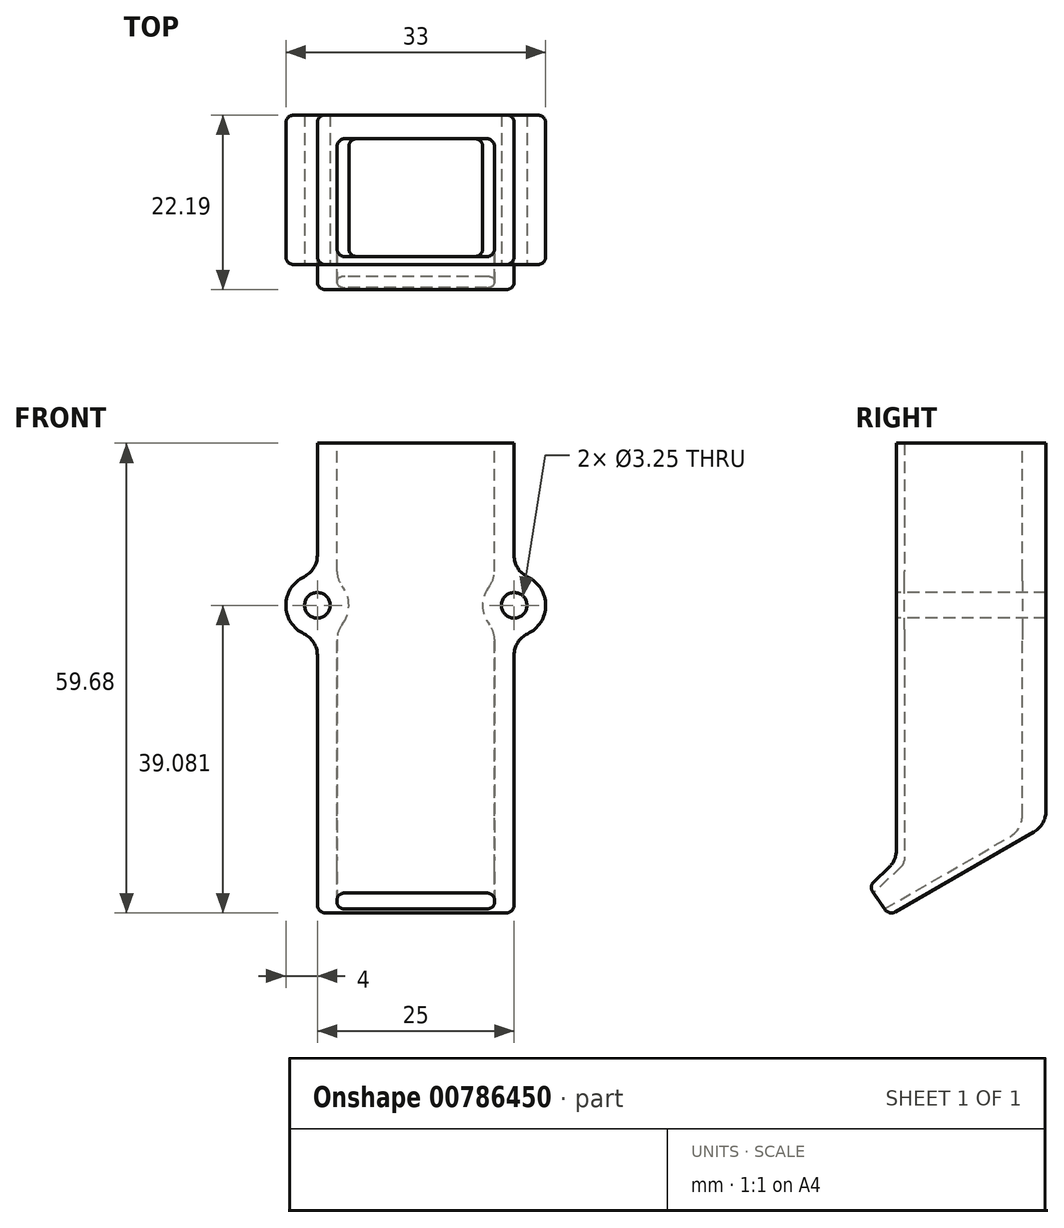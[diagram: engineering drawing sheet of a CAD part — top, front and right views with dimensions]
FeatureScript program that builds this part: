
annotation { "Feature Type Name" : "Feature", "Feature Type Description" : "" }
export const myFeature = defineFeature(function(context is Context, id is Id, definition is map)
    precondition{}
    {
        {
            var Q0;
            Q0=qCreatedBy(makeId("Right.planeOp"),FACE);
            var sketch = newSketch(context, id + "F0", { "sketchPlane" : qUnion([Q0])});
            skLineSegment(sketch, "E0", {"start": v(10.5, 0) * mm, "end": v(10.5, -48.5) * mm});
            skLineSegment(sketch, "E1", {"start": v(-8.5, 0) * mm, "end": v(-8.5, -53) * mm});
            skLineSegment(sketch, "E2", {"start": v(10.5, 0) * mm, "end": v(-8.5, 0) * mm});
            skLineSegment(sketch, "E3", {"start": v(-8.5, -53) * mm, "end": v(-12, -56.31) * mm});
            skLineSegment(sketch, "E4", {"start": v(-12, -56.31) * mm, "end": v(-9.42, -60) * mm});
            skLineSegment(sketch, "E5", {"start": v(-9.42, -60) * mm, "end": v(10.5, -48.5) * mm});
            skLineSegment(sketch, "E6", {"start": v(0, 3.25) * mm, "end": v(0, -60.76) * mm, "construction": true});
            skSolve(sketch);
        }
        {
            var Q0;
            Q0 = qSketchRegion(id + "F0", true);
            extrude(context, id + "F1", {"entities" : qUnion([Q0]), "endBound" : BoundingType.SYMMETRIC, "depth" : 25 * mm, "offsetDistance" : 25 * mm});
        }
        {
            var Q0;
            Q0=qCreatedBy(makeId("Right.planeOp"),FACE);
            var sketch = newSketch(context, id + "F2", { "sketchPlane" : qUnion([Q0])});
            skLineSegment(sketch, "E7", {"start": v(-7.5, 0) * mm, "end": v(-7.5, -53.43) * mm});
            skLineSegment(sketch, "E8", {"start": v(-7.5, -53.43) * mm, "end": v(-11.42, -57.14) * mm});
            skLineSegment(sketch, "E9", {"start": v(-11.42, -57.14) * mm, "end": v(-10, -59.18) * mm});
            skLineSegment(sketch, "E10", {"start": v(-10, -59.18) * mm, "end": v(7.5, -49.08) * mm});
            skLineSegment(sketch, "E11", {"start": v(7.5, -49.08) * mm, "end": v(7.5, 0) * mm});
            skLineSegment(sketch, "E12", {"start": v(7.5, 0) * mm, "end": v(-7.5, 0) * mm});
            skSolve(sketch);
        }
        {
            var Q0;
            Q0 = qSketchRegion(id + "F2", true);
            extrude(context, id + "F3", {"entities" : qUnion([Q0]), "operationType" : NewBodyOperationType.REMOVE, "endBound" : BoundingType.SYMMETRIC, "depth" : 20 * mm, "offsetDistance" : 25 * mm});
        }
        {
            var Q0;
            Q0=makeQuery(id+"F1.opExtrude","SWEPT_FACE",FACE,{"disambiguationData":[OSD([sQuery(id+"F0.wireOp",EDGE,"E1")])]});
            var sketch = newSketch(context, id + "F4", { "sketchPlane" : qUnion([Q0])});
            skCircle(sketch, "E13", {"center": v(12.5, -20.6) * mm, "radius": 4 * mm});
            skCircle(sketch, "E14", {"center": v(-12.5, -20.6) * mm, "radius": 4 * mm});
            skLineSegment(sketch, "E15", {"start": v(0, 4.77) * mm, "end": v(0, -64.34) * mm, "construction": true});
            skSolve(sketch);
        }
        {
            var Q0;
            Q0 = qSketchRegion(id + "F4", true);
            var Q1;
            Q1=makeQuery(id+"F1.opExtrude","SWEPT_FACE",FACE,{"disambiguationData":[OSD([sQuery(id+"F0.wireOp",EDGE,"E0")])]});
            extrude(context, id + "F5", {"entities" : qUnion([Q0]), "operationType" : NewBodyOperationType.ADD, "endBound" : BoundingType.UP_TO_SURFACE, "oppositeDirection" : true, "depth" : 25 * mm, "endBoundEntityFace" : qUnion([Q1]), "offsetDistance" : 25 * mm});
        }
        {
            var Q0;
            Q0=makeQuery(id+"F5.boolean.opBoolean","MERGE",FACE,{"derivedFrom":[makeQuery(id+"F1.opExtrude","SWEPT_FACE",FACE,{"disambiguationData":[OSD([sQuery(id+"F0.wireOp",EDGE,"E1")])]}),makeQuery(id+"F5.opExtrude","CAP_FACE",FACE,{"disambiguationData":[OSD([sQuery(id+"F4.wireOp",EDGE,"E13")])],"isStart":true}),makeQuery(id+"F5.opExtrude","CAP_FACE",FACE,{"disambiguationData":[OSD([sQuery(id+"F4.wireOp",EDGE,"E14")])],"isStart":true})]});
            var sketch = newSketch(context, id + "F6", { "sketchPlane" : qUnion([Q0])});
            skCircle(sketch, "E16.0", {"center": v(-12.5, -20.6) * mm, "radius": 1.62 * mm});
            skCircle(sketch, "E17.0", {"center": v(12.5, -20.6) * mm, "radius": 1.62 * mm});
            skSolve(sketch);
        }
        {
            var Q0;
            Q0 = qSketchRegion(id + "F6", true);
            var Q1;
            Q1=makeQuery(id+"F5.boolean.opBoolean","MERGE",FACE,{"derivedFrom":[makeQuery(id+"F1.opExtrude","SWEPT_FACE",FACE,{"disambiguationData":[OSD([sQuery(id+"F0.wireOp",EDGE,"E0")])]}),makeQuery(id+"F5.opExtrude","CAP_FACE",FACE,{"disambiguationData":[OSD([sQuery(id+"F4.wireOp",EDGE,"E13")])],"isStart":false}),makeQuery(id+"F5.opExtrude","CAP_FACE",FACE,{"disambiguationData":[OSD([sQuery(id+"F4.wireOp",EDGE,"E14")])],"isStart":false})]});
            extrude(context, id + "F7", {"entities" : qUnion([Q0]), "operationType" : NewBodyOperationType.REMOVE, "endBound" : BoundingType.UP_TO_SURFACE, "oppositeDirection" : true, "depth" : 25 * mm, "endBoundEntityFace" : qUnion([Q1]), "offsetDistance" : 25 * mm});
        }
        {
            var Q0;
            Q0=makeQuery(id+"F5.boolean.opBoolean","INTERSECT",EDGE,{"disambiguationData":[OD(0.0)],"derivedFrom":[makeQuery(id+"F1.opExtrude","CAP_FACE",FACE,{"disambiguationData":[OSD([sQuery(id+"F0.wireOp",EDGE,"E0"),sQuery(id+"F0.wireOp",EDGE,"E1"),sQuery(id+"F0.wireOp",EDGE,"E2"),sQuery(id+"F0.wireOp",EDGE,"E3"),sQuery(id+"F0.wireOp",EDGE,"E4"),sQuery(id+"F0.wireOp",EDGE,"E5")])],"isStart":true}),makeQuery(id+"F5.opExtrude","SWEPT_FACE",FACE,{"disambiguationData":[OSD([sQuery(id+"F4.wireOp",EDGE,"E14")])]})]});
            var Q1;
            Q1=makeQuery(id+"F5.boolean.opBoolean","INTERSECT",EDGE,{"disambiguationData":[OD(1.0)],"derivedFrom":[makeQuery(id+"F1.opExtrude","CAP_FACE",FACE,{"disambiguationData":[OSD([sQuery(id+"F0.wireOp",EDGE,"E0"),sQuery(id+"F0.wireOp",EDGE,"E1"),sQuery(id+"F0.wireOp",EDGE,"E2"),sQuery(id+"F0.wireOp",EDGE,"E3"),sQuery(id+"F0.wireOp",EDGE,"E4"),sQuery(id+"F0.wireOp",EDGE,"E5")])],"isStart":true}),makeQuery(id+"F5.opExtrude","SWEPT_FACE",FACE,{"disambiguationData":[OSD([sQuery(id+"F4.wireOp",EDGE,"E14")])]})]});
            var Q2;
            Q2=makeQuery(id+"F5.boolean.opBoolean","INTERSECT",EDGE,{"disambiguationData":[OD(0.0)],"derivedFrom":[makeQuery(id+"F1.opExtrude","CAP_FACE",FACE,{"disambiguationData":[OSD([sQuery(id+"F0.wireOp",EDGE,"E0"),sQuery(id+"F0.wireOp",EDGE,"E1"),sQuery(id+"F0.wireOp",EDGE,"E2"),sQuery(id+"F0.wireOp",EDGE,"E3"),sQuery(id+"F0.wireOp",EDGE,"E4"),sQuery(id+"F0.wireOp",EDGE,"E5")])],"isStart":false}),makeQuery(id+"F5.opExtrude","SWEPT_FACE",FACE,{"disambiguationData":[OSD([sQuery(id+"F4.wireOp",EDGE,"E13")])]})]});
            var Q3;
            Q3=makeQuery(id+"F5.boolean.opBoolean","INTERSECT",EDGE,{"disambiguationData":[OD(1.0)],"derivedFrom":[makeQuery(id+"F1.opExtrude","CAP_FACE",FACE,{"disambiguationData":[OSD([sQuery(id+"F0.wireOp",EDGE,"E0"),sQuery(id+"F0.wireOp",EDGE,"E1"),sQuery(id+"F0.wireOp",EDGE,"E2"),sQuery(id+"F0.wireOp",EDGE,"E3"),sQuery(id+"F0.wireOp",EDGE,"E4"),sQuery(id+"F0.wireOp",EDGE,"E5")])],"isStart":false}),makeQuery(id+"F5.opExtrude","SWEPT_FACE",FACE,{"disambiguationData":[OSD([sQuery(id+"F4.wireOp",EDGE,"E13")])]})]});
            var Q4;
            Q4=makeQuery(id+"F5.boolean.opBoolean","INTERSECT",EDGE,{"disambiguationData":[OD(1.0)],"derivedFrom":[makeQuery(id+"F3.boolean.opBoolean","COPY",FACE,{"derivedFrom":makeQuery(id+"F3.opExtrude","CAP_FACE",FACE,{"disambiguationData":[OSD([sQuery(id+"F2.wireOp",EDGE,"E7"),sQuery(id+"F2.wireOp",EDGE,"E8"),sQuery(id+"F2.wireOp",EDGE,"E9"),sQuery(id+"F2.wireOp",EDGE,"E10"),sQuery(id+"F2.wireOp",EDGE,"E11"),sQuery(id+"F2.wireOp",EDGE,"E12")])],"isStart":true})}),makeQuery(id+"F5.opExtrude","SWEPT_FACE",FACE,{"disambiguationData":[OSD([sQuery(id+"F4.wireOp",EDGE,"E14")])]})]});
            var Q5;
            Q5=makeQuery(id+"F5.boolean.opBoolean","INTERSECT",EDGE,{"disambiguationData":[OD(1.0)],"derivedFrom":[makeQuery(id+"F3.boolean.opBoolean","COPY",FACE,{"derivedFrom":makeQuery(id+"F3.opExtrude","CAP_FACE",FACE,{"disambiguationData":[OSD([sQuery(id+"F2.wireOp",EDGE,"E7"),sQuery(id+"F2.wireOp",EDGE,"E8"),sQuery(id+"F2.wireOp",EDGE,"E9"),sQuery(id+"F2.wireOp",EDGE,"E10"),sQuery(id+"F2.wireOp",EDGE,"E11"),sQuery(id+"F2.wireOp",EDGE,"E12")])],"isStart":false})}),makeQuery(id+"F5.opExtrude","SWEPT_FACE",FACE,{"disambiguationData":[OSD([sQuery(id+"F4.wireOp",EDGE,"E13")])]})]});
            var Q6;
            Q6=makeQuery(id+"F5.boolean.opBoolean","INTERSECT",EDGE,{"disambiguationData":[OD(0.0)],"derivedFrom":[makeQuery(id+"F3.boolean.opBoolean","COPY",FACE,{"derivedFrom":makeQuery(id+"F3.opExtrude","CAP_FACE",FACE,{"disambiguationData":[OSD([sQuery(id+"F2.wireOp",EDGE,"E7"),sQuery(id+"F2.wireOp",EDGE,"E8"),sQuery(id+"F2.wireOp",EDGE,"E9"),sQuery(id+"F2.wireOp",EDGE,"E10"),sQuery(id+"F2.wireOp",EDGE,"E11"),sQuery(id+"F2.wireOp",EDGE,"E12")])],"isStart":false})}),makeQuery(id+"F5.opExtrude","SWEPT_FACE",FACE,{"disambiguationData":[OSD([sQuery(id+"F4.wireOp",EDGE,"E13")])]})]});
            var Q7;
            Q7=makeQuery(id+"F5.boolean.opBoolean","INTERSECT",EDGE,{"disambiguationData":[OD(0.0)],"derivedFrom":[makeQuery(id+"F3.boolean.opBoolean","COPY",FACE,{"derivedFrom":makeQuery(id+"F3.opExtrude","CAP_FACE",FACE,{"disambiguationData":[OSD([sQuery(id+"F2.wireOp",EDGE,"E7"),sQuery(id+"F2.wireOp",EDGE,"E8"),sQuery(id+"F2.wireOp",EDGE,"E9"),sQuery(id+"F2.wireOp",EDGE,"E10"),sQuery(id+"F2.wireOp",EDGE,"E11"),sQuery(id+"F2.wireOp",EDGE,"E12")])],"isStart":true})}),makeQuery(id+"F5.opExtrude","SWEPT_FACE",FACE,{"disambiguationData":[OSD([sQuery(id+"F4.wireOp",EDGE,"E14")])]})]});
            var Q8;
            Q8=makeQuery(id+"F3.boolean.opBoolean","COPY",EDGE,{"derivedFrom":makeQuery(id+"F3.opExtrude","SWEPT_EDGE",EDGE,{"disambiguationData":[OSD([sQuery(id+"F2.wireOp",EDGE,"E10"),sQuery(id+"F2.wireOp",EDGE,"E11")])]})});
            var Q9;
            Q9=makeQuery(id+"F1.opExtrude","SWEPT_EDGE",EDGE,{"disambiguationData":[OSD([sQuery(id+"F0.wireOp",EDGE,"E1"),sQuery(id+"F0.wireOp",EDGE,"E3")])]});
            var Q10;
            Q10=makeQuery(id+"F1.opExtrude","SWEPT_EDGE",EDGE,{"disambiguationData":[OSD([sQuery(id+"F0.wireOp",EDGE,"E0"),sQuery(id+"F0.wireOp",EDGE,"E5")])]});
            fillet(context, id + "F8", {"entities" : qUnion([Q0, Q1, Q2, Q3, Q4, Q5, Q6, Q7, Q8, Q9, Q10]), "tangentPropagation" : true, "radius" : 3 * mm, "defaultsChanged" : false, "vertexSettings" : [], "allowEdgeOverflow" : false});
        }
        {
            var Q0;
            {var subQ0=sQuery(id+"F2.wireOp",EDGE,"E7");Q0=makeQuery(id+"F5.boolean.opBoolean","SPLIT",EDGE,{"disambiguationData":[TD([makeQuery(id+"F1.opExtrude","SWEPT_FACE",FACE,{"disambiguationData":[OSD([sQuery(id+"F0.wireOp",EDGE,"E2")])]})])],"derivedFrom":makeQuery(id+"F3.boolean.opBoolean","COPY",EDGE,{"derivedFrom":makeQuery(id+"F3.opExtrude","CAP_EDGE",EDGE,{"disambiguationData":[OSD([subQ0])],"isStart":false})})});}
            var Q1;
            {var subQ0=sQuery(id+"F2.wireOp",EDGE,"E7");Q1=makeQuery(id+"F5.boolean.opBoolean","SPLIT",EDGE,{"disambiguationData":[TD([makeQuery(id+"F1.opExtrude","SWEPT_FACE",FACE,{"disambiguationData":[OSD([sQuery(id+"F0.wireOp",EDGE,"E2")])]})])],"derivedFrom":makeQuery(id+"F3.boolean.opBoolean","COPY",EDGE,{"derivedFrom":makeQuery(id+"F3.opExtrude","CAP_EDGE",EDGE,{"disambiguationData":[OSD([subQ0])],"isStart":true})})});}
            var Q2;
            {var subQ0=sQuery(id+"F2.wireOp",EDGE,"E11");Q2=makeQuery(id+"F5.boolean.opBoolean","SPLIT",EDGE,{"disambiguationData":[TD([makeQuery(id+"F1.opExtrude","SWEPT_FACE",FACE,{"disambiguationData":[OSD([sQuery(id+"F0.wireOp",EDGE,"E2")])]})])],"derivedFrom":makeQuery(id+"F3.boolean.opBoolean","COPY",EDGE,{"derivedFrom":makeQuery(id+"F3.opExtrude","CAP_EDGE",EDGE,{"disambiguationData":[OSD([subQ0])],"isStart":false})})});}
            var Q3;
            {var subQ0=sQuery(id+"F2.wireOp",EDGE,"E11");Q3=makeQuery(id+"F5.boolean.opBoolean","SPLIT",EDGE,{"disambiguationData":[TD([makeQuery(id+"F1.opExtrude","SWEPT_FACE",FACE,{"disambiguationData":[OSD([sQuery(id+"F0.wireOp",EDGE,"E2")])]})])],"derivedFrom":makeQuery(id+"F3.boolean.opBoolean","COPY",EDGE,{"derivedFrom":makeQuery(id+"F3.opExtrude","CAP_EDGE",EDGE,{"disambiguationData":[OSD([subQ0])],"isStart":true})})});}
            var Q4;
            Q4=makeQuery(id+"F3.boolean.opBoolean","COPY",EDGE,{"derivedFrom":makeQuery(id+"F3.opExtrude","CAP_EDGE",EDGE,{"disambiguationData":[OSD([sQuery(id+"F2.wireOp",EDGE,"E10")])],"isStart":true})});
            var Q5;
            Q5=makeQuery(id+"F3.boolean.opBoolean","COPY",EDGE,{"derivedFrom":makeQuery(id+"F3.opExtrude","CAP_EDGE",EDGE,{"disambiguationData":[OSD([sQuery(id+"F2.wireOp",EDGE,"E10")])],"isStart":false})});
            var Q6;
            Q6=makeQuery(id+"F3.boolean.opBoolean","COPY",EDGE,{"derivedFrom":makeQuery(id+"F3.opExtrude","CAP_EDGE",EDGE,{"disambiguationData":[OSD([sQuery(id+"F2.wireOp",EDGE,"E8")])],"isStart":false})});
            var Q7;
            Q7=makeQuery(id+"F3.boolean.opBoolean","COPY",EDGE,{"derivedFrom":makeQuery(id+"F3.opExtrude","CAP_EDGE",EDGE,{"disambiguationData":[OSD([sQuery(id+"F2.wireOp",EDGE,"E8")])],"isStart":true})});
            var Q8;
            Q8=makeQuery(id+"F3.boolean.opBoolean","COPY",EDGE,{"derivedFrom":makeQuery(id+"F3.opExtrude","SWEPT_EDGE",EDGE,{"disambiguationData":[OSD([sQuery(id+"F2.wireOp",EDGE,"E7"),sQuery(id+"F2.wireOp",EDGE,"E8")])]})});
            var Q9;
            {var subQ0=sQuery(id+"F0.wireOp",EDGE,"E3");var subQ1=sQuery(id+"F0.wireOp",EDGE,"E1");var subQ2=makeQuery(id+"F1.opExtrude","SWEPT_FACE",FACE,{"disambiguationData":[OSD([subQ1])]});var subQ4=makeQuery(id+"F1.opExtrude","CAP_FACE",FACE,{"disambiguationData":[OSD([sQuery(id+"F0.wireOp",EDGE,"E0"),subQ1,sQuery(id+"F0.wireOp",EDGE,"E2"),subQ0,sQuery(id+"F0.wireOp",EDGE,"E4"),sQuery(id+"F0.wireOp",EDGE,"E5")])],"isStart":true});Q9=makeQuery(id+"F5.boolean.opBoolean","SPLIT",EDGE,{"disambiguationData":[topologyDisambiguationEdgeConnected([subQ4,subQ2]),TD([makeQuery(id+"F1.opExtrude","SWEPT_FACE",FACE,{"disambiguationData":[OSD([subQ0])]})])],"derivedFrom":makeQuery(id+"F1.opExtrude","CAP_EDGE",EDGE,{"disambiguationData":[OSD([subQ1])],"isStart":true})});}
            var Q10;
            Q10=makeQuery(id+"F5.opExtrude","CAP_EDGE",EDGE,{"disambiguationData":[OSD([sQuery(id+"F4.wireOp",EDGE,"E14")])],"isStart":true});
            var Q11;
            {var subQ0=sQuery(id+"F0.wireOp",EDGE,"E2");var subQ1=sQuery(id+"F0.wireOp",EDGE,"E1");var subQ2=makeQuery(id+"F1.opExtrude","SWEPT_FACE",FACE,{"disambiguationData":[OSD([subQ1])]});var subQ4=makeQuery(id+"F1.opExtrude","CAP_FACE",FACE,{"disambiguationData":[OSD([sQuery(id+"F0.wireOp",EDGE,"E0"),subQ1,subQ0,sQuery(id+"F0.wireOp",EDGE,"E3"),sQuery(id+"F0.wireOp",EDGE,"E4"),sQuery(id+"F0.wireOp",EDGE,"E5")])],"isStart":true});Q11=makeQuery(id+"F5.boolean.opBoolean","SPLIT",EDGE,{"disambiguationData":[topologyDisambiguationEdgeConnected([subQ4,subQ2]),TD([makeQuery(id+"F1.opExtrude","SWEPT_FACE",FACE,{"disambiguationData":[OSD([subQ0])]})])],"derivedFrom":makeQuery(id+"F1.opExtrude","CAP_EDGE",EDGE,{"disambiguationData":[OSD([subQ1])],"isStart":true})});}
            var Q12;
            Q12=makeQuery(id+"F1.opExtrude","CAP_EDGE",EDGE,{"disambiguationData":[OSD([sQuery(id+"F0.wireOp",EDGE,"E4")])],"isStart":true});
            var Q13;
            Q13=makeQuery(id+"F1.opExtrude","CAP_EDGE",EDGE,{"disambiguationData":[OSD([sQuery(id+"F0.wireOp",EDGE,"E5")])],"isStart":true});
            var Q14;
            {var subQ0=sQuery(id+"F0.wireOp",EDGE,"E5");var subQ1=sQuery(id+"F0.wireOp",EDGE,"E0");Q14=makeQuery(id+"F5.boolean.opBoolean","SPLIT",EDGE,{"disambiguationData":[TD([makeQuery(id+"F1.opExtrude","SWEPT_FACE",FACE,{"disambiguationData":[OSD([subQ0])]})])],"derivedFrom":makeQuery(id+"F1.opExtrude","CAP_EDGE",EDGE,{"disambiguationData":[OSD([subQ1])],"isStart":true})});}
            var Q15;
            {var subQ1=sQuery(id+"F0.wireOp",EDGE,"E5");var subQ2=sQuery(id+"F0.wireOp",EDGE,"E0");Q15=makeQuery(id+"F5.boolean.opBoolean","SPLIT",EDGE,{"disambiguationData":[TD([makeQuery(id+"F1.opExtrude","SWEPT_FACE",FACE,{"disambiguationData":[OSD([subQ1])]})])],"derivedFrom":makeQuery(id+"F1.opExtrude","CAP_EDGE",EDGE,{"disambiguationData":[OSD([subQ2])],"isStart":false})});}
            var Q16;
            Q16=makeQuery(id+"F1.opExtrude","SWEPT_EDGE",EDGE,{"disambiguationData":[OSD([sQuery(id+"F0.wireOp",EDGE,"E0"),sQuery(id+"F0.wireOp",EDGE,"E5")])]});
            var Q17;
            {var subQ0=sQuery(id+"F0.wireOp",EDGE,"E3");var subQ2=sQuery(id+"F0.wireOp",EDGE,"E1");var subQ3=makeQuery(id+"F1.opExtrude","SWEPT_FACE",FACE,{"disambiguationData":[OSD([subQ2])]});var subQ4=makeQuery(id+"F1.opExtrude","CAP_FACE",FACE,{"disambiguationData":[OSD([sQuery(id+"F0.wireOp",EDGE,"E0"),subQ2,sQuery(id+"F0.wireOp",EDGE,"E2"),subQ0,sQuery(id+"F0.wireOp",EDGE,"E4"),sQuery(id+"F0.wireOp",EDGE,"E5")])],"isStart":false});Q17=makeQuery(id+"F5.boolean.opBoolean","SPLIT",EDGE,{"disambiguationData":[topologyDisambiguationEdgeConnected([subQ4,subQ3]),TD([makeQuery(id+"F1.opExtrude","SWEPT_FACE",FACE,{"disambiguationData":[OSD([subQ0])]})])],"derivedFrom":makeQuery(id+"F1.opExtrude","CAP_EDGE",EDGE,{"disambiguationData":[OSD([subQ2])],"isStart":false})});}
            var Q18;
            Q18=makeQuery(id+"F5.opExtrude","CAP_EDGE",EDGE,{"disambiguationData":[OSD([sQuery(id+"F4.wireOp",EDGE,"E13")])],"isStart":true});
            var Q19;
            Q19=makeQuery(id+"F1.opExtrude","CAP_EDGE",EDGE,{"disambiguationData":[OSD([sQuery(id+"F0.wireOp",EDGE,"E5")])],"isStart":false});
            var Q20;
            Q20=makeQuery(id+"F1.opExtrude","SWEPT_EDGE",EDGE,{"disambiguationData":[OSD([sQuery(id+"F0.wireOp",EDGE,"E3"),sQuery(id+"F0.wireOp",EDGE,"E4")])]});
            var Q21;
            Q21=makeQuery(id+"F1.opExtrude","CAP_EDGE",EDGE,{"disambiguationData":[OSD([sQuery(id+"F0.wireOp",EDGE,"E4")])],"isStart":false});
            var Q22;
            Q22=makeQuery(id+"F1.opExtrude","SWEPT_EDGE",EDGE,{"disambiguationData":[OSD([sQuery(id+"F0.wireOp",EDGE,"E4"),sQuery(id+"F0.wireOp",EDGE,"E5")])]});
            fillet(context, id + "F9", {"entities" : qUnion([Q0, Q1, Q2, Q3, Q4, Q5, Q6, Q7, Q8, Q9, Q10, Q11, Q12, Q13, Q14, Q15, Q16, Q17, Q18, Q19, Q20, Q21, Q22]), "tangentPropagation" : true, "radius" : 1 * mm, "defaultsChanged" : false, "vertexSettings" : [], "allowEdgeOverflow" : false});
        }
    });
